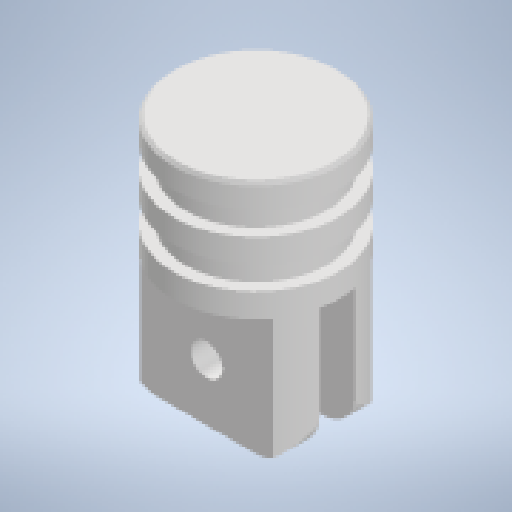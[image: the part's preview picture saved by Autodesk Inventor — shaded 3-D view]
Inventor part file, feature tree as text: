
AUTODESK INVENTOR PART (.ipt)
format: ipt  version: 2023 (Build 270158000, 158)  size: 332,800 bytes
history: native  units: in
note: dims shown in document units (in); Inventor stores cm internally (conversion verified against a paired STEP export)
features: sketch x4, extrude x3, revolve x1, chamfer x1
ambient origin geometry x8: Origin, YZ Plane, XZ Plane, XY Plane, X Axis, Y Axis, Z Axis, Center Point
bodies: Body1 (feature_tree)
feature tree (9):
  revolve  "Revolution1"  [1 undecoded]
  chamfer  "Chamfer1"  Angle=360.0deg  [1 undecoded]
  sketch  "Sketch10"  dims[d17=0.1875in]
  extrude  "Extrusion6"  Depth=0.125in TaperAngle=45.0deg
  extrude  "Extrusion7"  Depth=0.125in
  extrude  "Extrusion8"  Depth=0.125in TaperAngle=0.0deg
  sketch  "Sketch5"  dims[d15=0.0938in d16=0.1875in]
  sketch  "Sketch12"  dims[d18=0.1875in]
  sketch  "Sketch13"  dims[d19=0.1875in d20=360.0deg d24=0.025in d25=0.125in d26=45.0deg d38=0.188in d65=1.0in d66=0.0in d68=0.25in d69=0.25in d70=0.25in d71=1.0in d72=0.0in d73=0.281in d74=0.0in d45=0.5in d46=0.0344in d47=0.5in d48=0.0344in d75=0.5in d76=0.0344in]
note: 2 required parameter values undecoded (feature->parameter linkage not recoverable at this tier; creation-order binding heuristic only, values carry confidence <= 0.55)